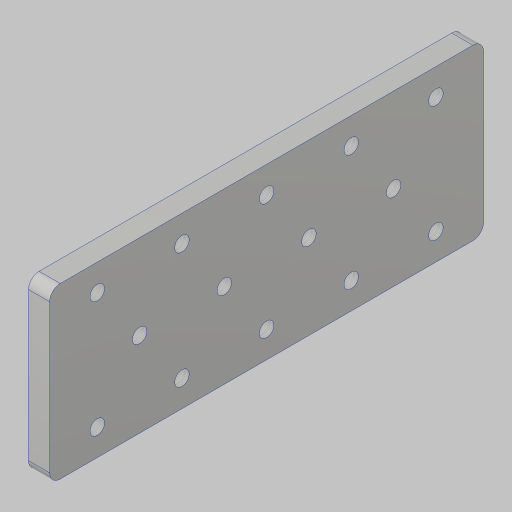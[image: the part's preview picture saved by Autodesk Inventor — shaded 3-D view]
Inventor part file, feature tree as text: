
AUTODESK INVENTOR PART (.ipt)
format: ipt  version: 2023.5 (Build 275446000, 446)  size: 145,408 bytes
history: native  units: in
note: dims shown in document units (in); Inventor stores cm internally (conversion verified against a paired STEP export)
features: sketch x2, extrude x1, hole x1, fillet x1, projected_geometry x1
ambient origin geometry x8: Origin, YZ Plane, XZ Plane, XY Plane, X Axis, Y Axis, Z Axis, Center Point
bodies: Solid1 (feature_tree)
feature tree (6):
  extrude  "Extrusion1"  Depth=2.0in
  hole  "Hole1"  [1 undecoded]
  fillet  "Fillet1"  Radius=0.5625in
  sketch  "Sketch1"  dims[d0=5.125in d1=2.0in]
  sketch  "Sketch2"  dims[d2=0.25in d3=0.5in d4=0.0in d5=0.0in d6=1.375in d7=0.5625in d8=0.5in d9=1.9685in d11=1.0in d12=0.3937in d14=1.0in d16=0.171in d17=0.432in d18=0.385in d19=0.25in d20=0.5635in d21=1.0in d22=0.8108in d23=0.125in]
  projected_geometry  "Project Cut Edges1"
note: 1 required parameter value undecoded (feature->parameter linkage not recoverable at this tier; creation-order binding heuristic only, values carry confidence <= 0.55)
